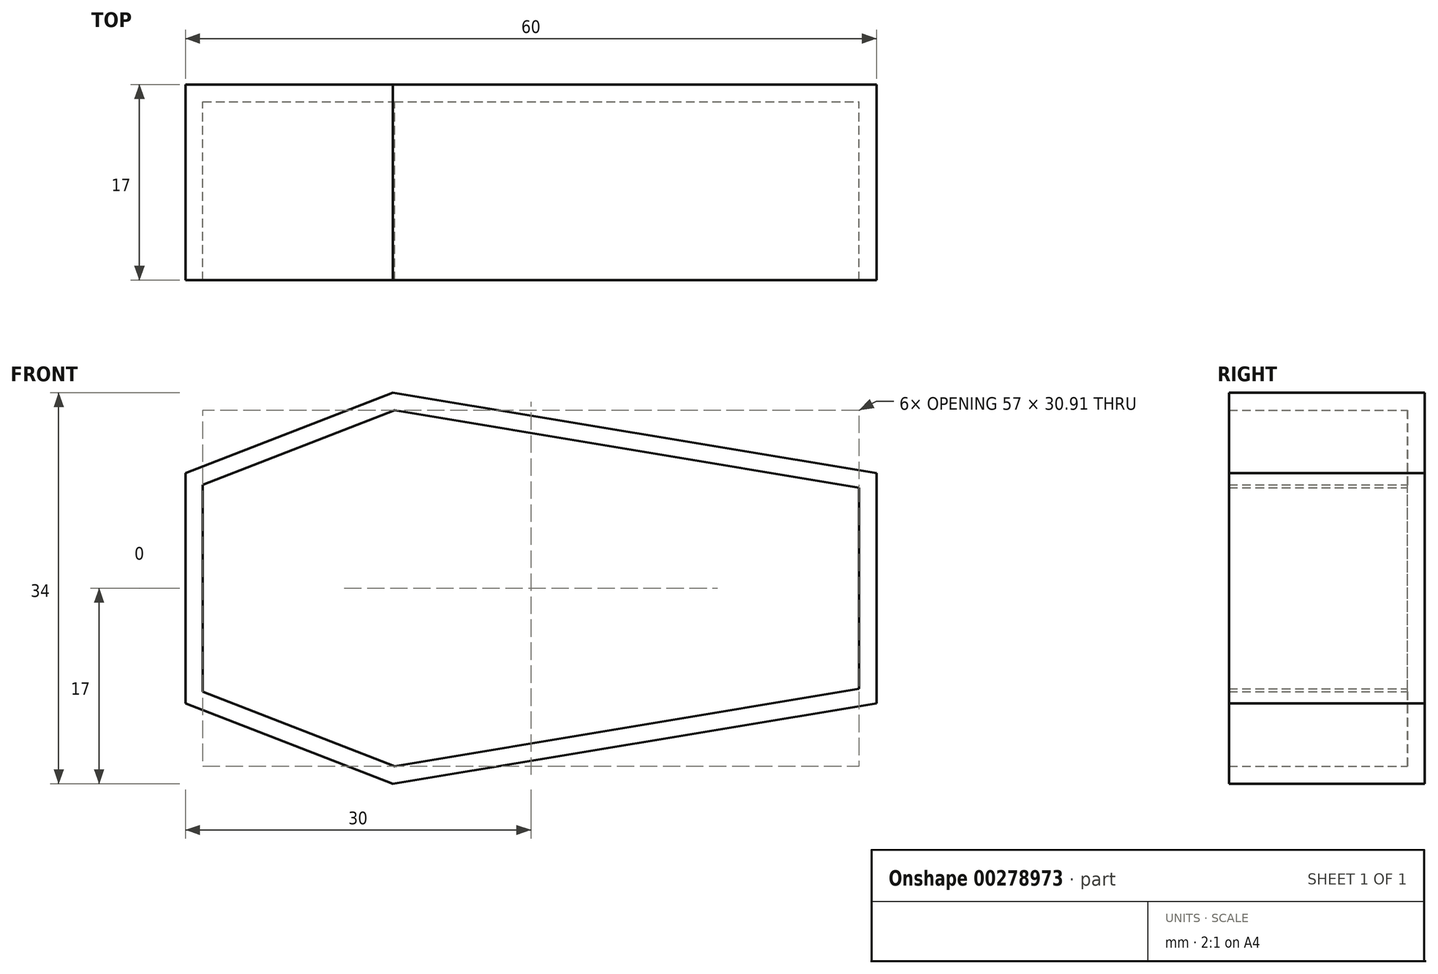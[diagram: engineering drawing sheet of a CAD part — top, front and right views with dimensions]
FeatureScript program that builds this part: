
annotation { "Feature Type Name" : "Feature", "Feature Type Description" : "" }
export const myFeature = defineFeature(function(context is Context, id is Id, definition is map)
    precondition{}
    {
        {
            var Q0;
            Q0=qCreatedBy(makeId("Front.planeOp"),FACE);
            var sketch = newSketch(context, id + "F0", { "sketchPlane" : qUnion([Q0])});
            skLineSegment(sketch, "E0.bottom", {"start": v(0, 0) * mm, "end": v(60, 0) * mm});
            skLineSegment(sketch, "E0.top", {"start": v(0, 20) * mm, "end": v(60, 20) * mm});
            skLineSegment(sketch, "E0.left", {"start": v(0, 0) * mm, "end": v(0, 20) * mm});
            skLineSegment(sketch, "E0.right", {"start": v(60, 0) * mm, "end": v(60, 20) * mm});
            skLineSegment(sketch, "E1", {"start": v(18, 20) * mm, "end": v(18, 0) * mm});
            skLineSegment(sketch, "E2", {"start": v(18, 20) * mm, "end": v(18, 27) * mm});
            skLineSegment(sketch, "E3", {"start": v(18, 0) * mm, "end": v(18, -7) * mm});
            skLineSegment(sketch, "E4", {"start": v(0, 20) * mm, "end": v(18, 27) * mm});
            skLineSegment(sketch, "E5", {"start": v(0, 0) * mm, "end": v(18, -7) * mm});
            skLineSegment(sketch, "E6", {"start": v(18, -7) * mm, "end": v(60, 0) * mm});
            skLineSegment(sketch, "E7", {"start": v(18, 27) * mm, "end": v(60, 20) * mm});
            skSolve(sketch);
        }
        {
            var Q0;
            Q0 = qSketchRegion(id + "F0", true);
            extrude(context, id + "F1", {"entities" : qUnion([Q0]), "depth" : 17 * mm});
        }
        {
            var Q0;
            Q0=makeQuery(id+"F1.opExtrude","CAP_FACE",FACE,{"disambiguationData":[OSD([sQuery(id+"F0.wireOp",EDGE,"E0.left"),sQuery(id+"F0.wireOp",EDGE,"E0.right"),sQuery(id+"F0.wireOp",EDGE,"E4"),sQuery(id+"F0.wireOp",EDGE,"E5"),sQuery(id+"F0.wireOp",EDGE,"E6"),sQuery(id+"F0.wireOp",EDGE,"E7")])],"isStart":false});
            shell(context, id + "F2", {"entities" : qUnion([Q0]), "thickness" : 1.5 * mm});
        }
    });
